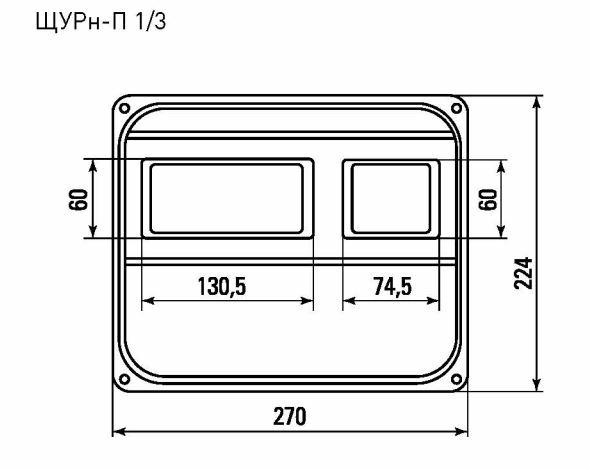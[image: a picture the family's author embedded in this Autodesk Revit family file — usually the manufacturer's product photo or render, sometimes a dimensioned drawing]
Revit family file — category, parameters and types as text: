
# Revit family: EKF_EE_ЩМП_RAL 3001_IP31_PROxima
name_source: partatom
category: Электрооборудование
units: mm (PartAtom-declared; Revit-internal decimal feet)

## family parameters
Всегда вертикально = Да
На основе рабочей плоскости = Нет
Общий = Нет
При загрузке вырезать с полостями = Нет
Размер круглого соединителя = Использовать диаметр
Тип детали = Силовой щит
Точка расчета площади = Да

## types (6) — shared parameters
ADSK_Единица измерения = компл.
ADSK_Завод-изготовитель = EKF
ADSK_Классификация нагрузок = Прочее
ADSK_Количество = 1
ADSK_Количество фаз = 3
ADSK_Коэффициент мощности = 1
ADSK_Материал = RAL 3001
ADSK_Напряжение = 400 В
ADSK_Номинальная мощность = 0 Вт
ADSK_Полная мощность = 0 В·А
ADSK_Ток = 125 А
Изготовитель = EKF
Серия номенклатуры = Basic
Степень защиты IP = IP54
ТВ = EKF
Тип установки = Навесной
УГО_Реальный размер = Нет
zero-valued in all types: Количество DIN-реек, Количество модулей на DIN-рейке, Максимальное количество модулей

## per-type parameters (varying)
| type | ADSK_Код изделия | ADSK_Марка | ADSK_Масса | ADSK_Наименование | ADSK_Обозначение | ADSK_Размер_Высота | ADSK_Размер_Глубина | ADSK_Размер_Ширина | Описание | Тип |
| ЩМПг- 40.30.22 (ЩРНМ-1) RAL 3001 IP54 EKF PROxima | mb24-1-3001 | ЩМПг- 40.30.22 (ЩРНМ-1) IP54 | 7.2 | Щит с монтажной панелью ЩМПг- 40.30.22 (ЩРНМ-1) RAL 3001 IP54 EKF PROxima | ЩМПг- 40.30.22 (ЩРНМ-1) IP54 | 400 мм | 220 мм | 300 мм | Щит с монтажной панелью ЩМПг- 40.30.22 (ЩРНМ-1) RAL 3001 IP54 EKF PROxima | 107 мм |
| ЩМПг- 50.40.22 (ЩРНМ-2) RAL 3001 IP54 EKF PROxima | mb24-2-3001 | ЩМПг- 50.40.22 (ЩРНМ-2) IP54 | 11.39 | Щит с монтажной панелью ЩМПг- 50.40.22 (ЩРНМ-2) RAL 3001 IP54 EKF PROxima | ЩМПг- 50.40.22 (ЩРНМ-2) IP54 | 500 мм | 220 мм | 400 мм | Щит с монтажной панелью ЩМПг- 50.40.22 (ЩРНМ-2) RAL 3001 IP54 EKF PROxima | 108 мм |
| ЩМПг- 60.60.25 RAL 3001 IP54 EKF PROxima | mb24-06-3001 | ЩМПг- 60.60.25 RAL 3001 IP54 | 15 | Щит с монтажной панелью ЩМПг- 60.60.25 RAL 3001 IP54 EKF PROxima | ЩМПг- 60.60.25 RAL 3001 IP54 | 600 мм | 250 мм | 600 мм | Щит с монтажной панелью ЩМПг- 60.60.25 RAL 3001 IP54 EKF PROxima | 109 мм |
| ЩМПг- 65.50.22 (ЩРНМ-3) RAL 3001 IP54 EKF PROxima | mb24-3-3001 | ЩМПг- 65.50.22 (ЩРНМ-3) IP54 | 15.76 | Щит с монтажной панелью ЩМПг- 65.50.22 (ЩРНМ-3) RAL 3001 IP54 EKF PROxima | ЩМПг- 65.50.22 (ЩРНМ-3) IP54 | 650 мм | 220 мм | 500 мм | Щит с монтажной панелью ЩМПг- 65.50.22 (ЩРНМ-3) RAL 3001 IP54 EKF PROxima | 110 мм |
| ЩМПг- 80.60.25 (ЩРНМ-4) RAL 3001 IP54 EKF PROxima | mb24-4-3001 | ЩМПг- 80.60.25 (ЩРНМ-4) IP54 | 24.15 | Щит с монтажной панелью ЩМПг- 80.60.25 (ЩРНМ-4) RAL 3001 IP54 EKF PROxima | ЩМПг- 80.60.25 (ЩРНМ-4) IP54 | 800 мм | 250 мм | 600 мм | Щит с монтажной панелью ЩМПг- 80.60.25 (ЩРНМ-4) RAL 3001 IP54 EKF PROxima | 111 мм |
| ЩМПг-100.65.30 (ЩРНМ-5) RAL 3001 IP54 EKF PROxima | mb24-5-3001 | ЩМПг-100.65.30 (ЩРНМ-5) IP54 | 33.03 | Щит с монтажной панелью ЩМПг-100.65.30 (ЩРНМ-5) RAL 3001 IP54 EKF PROxima | ЩМПг-100.65.30 (ЩРНМ-5) IP54 | 1000 мм | 300 мм | 650 мм | Щит с монтажной панелью ЩМПг-100.65.30 (ЩРНМ-5) RAL 3001 IP54 EKF PROxima | 112 мм |
